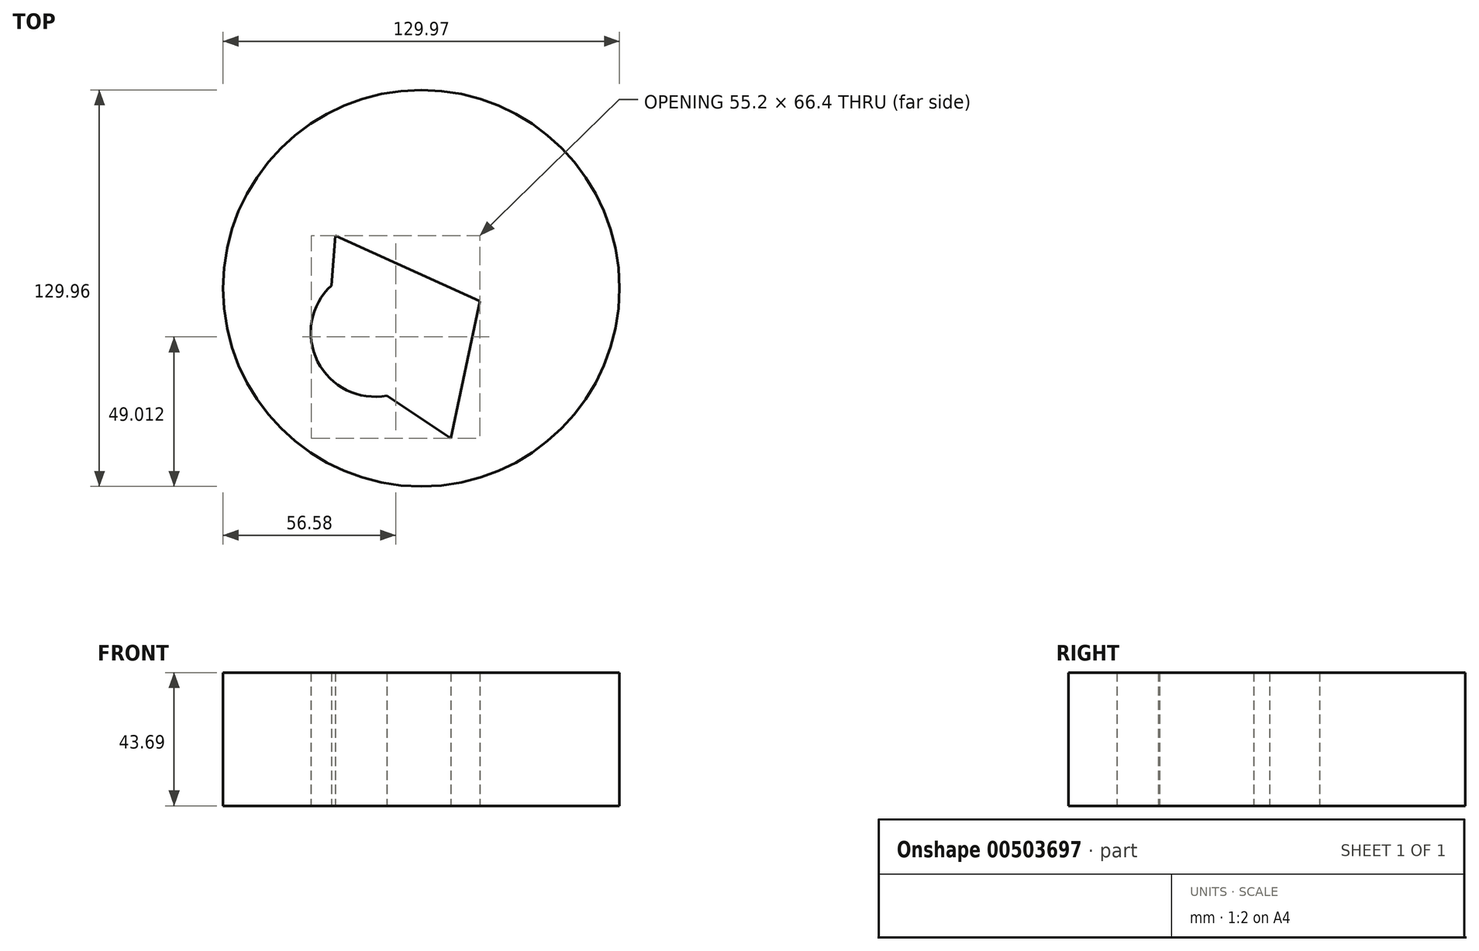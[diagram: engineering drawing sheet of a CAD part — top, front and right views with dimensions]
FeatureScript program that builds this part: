
annotation { "Feature Type Name" : "Feature", "Feature Type Description" : "" }
export const myFeature = defineFeature(function(context is Context, id is Id, definition is map)
    precondition{}
    {
        {
            var Q0;
            Q0=qCreatedBy(makeId("Top.planeOp"),FACE);
            var sketch = newSketch(context, id + "F0", { "sketchPlane" : qUnion([Q0])});
            skLineSegment(sketch, "E0", {"start": v(-30.97, 0) * mm, "end": v(-27.71, 38.92) * mm});
            skLineSegment(sketch, "E1", {"start": v(-27.71, 38.92) * mm, "end": v(19.6, 17.4) * mm});
            skLineSegment(sketch, "E2", {"start": v(19.6, 17.4) * mm, "end": v(10.03, -27.48) * mm});
            skLineSegment(sketch, "E3", {"start": v(10.03, -27.48) * mm, "end": v(-30.97, 0) * mm});
            skCircle(sketch, "E4", {"center": v(-14.79, 7.16) * mm, "radius": 21.02 * mm});
            skCircle(sketch, "E5", {"center": v(0.41, 21.69) * mm, "radius": 64.98 * mm});
            skSolve(sketch);
        }
        {
            var Q0;
            Q0 = qSketchRegion(id + "F0", true);
            extrude(context, id + "F1", {"entities" : qUnion([Q0]), "depth" : 43.69 * mm});
        }
    });
